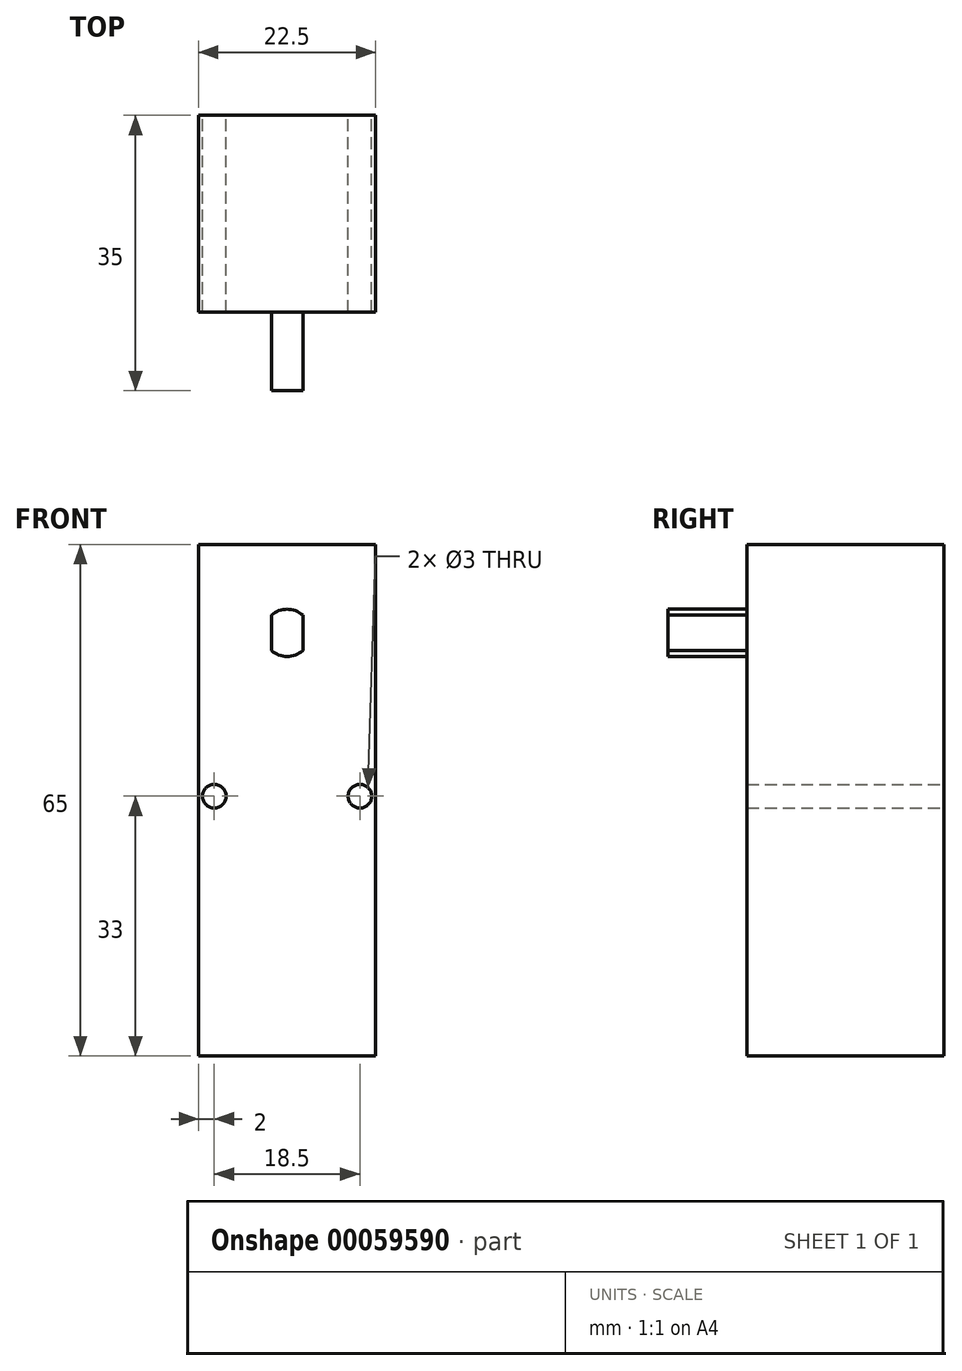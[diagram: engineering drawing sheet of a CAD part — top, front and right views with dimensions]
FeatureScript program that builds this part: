
annotation { "Feature Type Name" : "Feature", "Feature Type Description" : "" }
export const myFeature = defineFeature(function(context is Context, id is Id, definition is map)
    precondition{}
    {
        {
            var Q0;
            Q0=qCreatedBy(makeId("Front.planeOp"),FACE);
            var sketch = newSketch(context, id + "F0", { "sketchPlane" : qUnion([Q0])});
            skLineSegment(sketch, "E0.bottom", {"start": v(-11.25, 32.5) * mm, "end": v(11.25, 32.5) * mm});
            skLineSegment(sketch, "E0.top", {"start": v(-11.25, -32.5) * mm, "end": v(11.25, -32.5) * mm});
            skLineSegment(sketch, "E0.left", {"start": v(-11.25, 32.5) * mm, "end": v(-11.25, -32.5) * mm});
            skLineSegment(sketch, "E0.right", {"start": v(11.25, 32.5) * mm, "end": v(11.25, -32.5) * mm});
            skPoint(sketch, "E0.middle", {"position": v(0, 0) * mm});
            skCircle(sketch, "E1", {"center": v(9.25, 0.5) * mm, "radius": 1.5 * mm});
            skCircle(sketch, "E2.MirrorC", {"center": v(-9.25, 0.5) * mm, "radius": 1.5 * mm});
            skSolve(sketch);
        }
        {
            var Q0;
            Q0=qSketchRegion(id+"F0",true);
            extrude(context, id + "F1", {"entities" : qUnion([Q0]), "depth" : 25 * mm});
        }
        {
            var Q0;
            Q0=makeQuery(id+"F1.opExtrude","CAP_FACE",FACE,{"disambiguationData":[OSD([sQuery(id+"F0.wireOp",EDGE,"E0.bottom"),sQuery(id+"F0.wireOp",EDGE,"E0.top"),sQuery(id+"F0.wireOp",EDGE,"E0.left"),sQuery(id+"F0.wireOp",EDGE,"E0.right"),sQuery(id+"F0.wireOp",EDGE,"E1"),sQuery(id+"F0.wireOp",EDGE,"E2.MirrorC")])],"isStart":false});
            var sketch = newSketch(context, id + "F2", { "sketchPlane" : qUnion([Q0])});
            skArc(sketch, "E3", {"start": v(-2, 19.01) * mm, "mid": v(0, 18.25) * mm, "end": v(2, 19.01) * mm});
            skLineSegment(sketch, "E4.left", {"start": v(-2, 23.49) * mm, "end": v(-2, 19.01) * mm});
            skLineSegment(sketch, "E4.right", {"start": v(2, 23.49) * mm, "end": v(2, 19.01) * mm});
            skArc(sketch, "E5.trimOffspring", {"start": v(2, 23.49) * mm, "mid": v(0, 24.25) * mm, "end": v(-2, 23.49) * mm});
            skSolve(sketch);
        }
        {
            var Q0;
            Q0=qSketchRegion(id+"F2",true);
            extrude(context, id + "F3", {"entities" : qUnion([Q0]), "operationType" : NewBodyOperationType.ADD, "depth" : 10 * mm});
        }
    });
